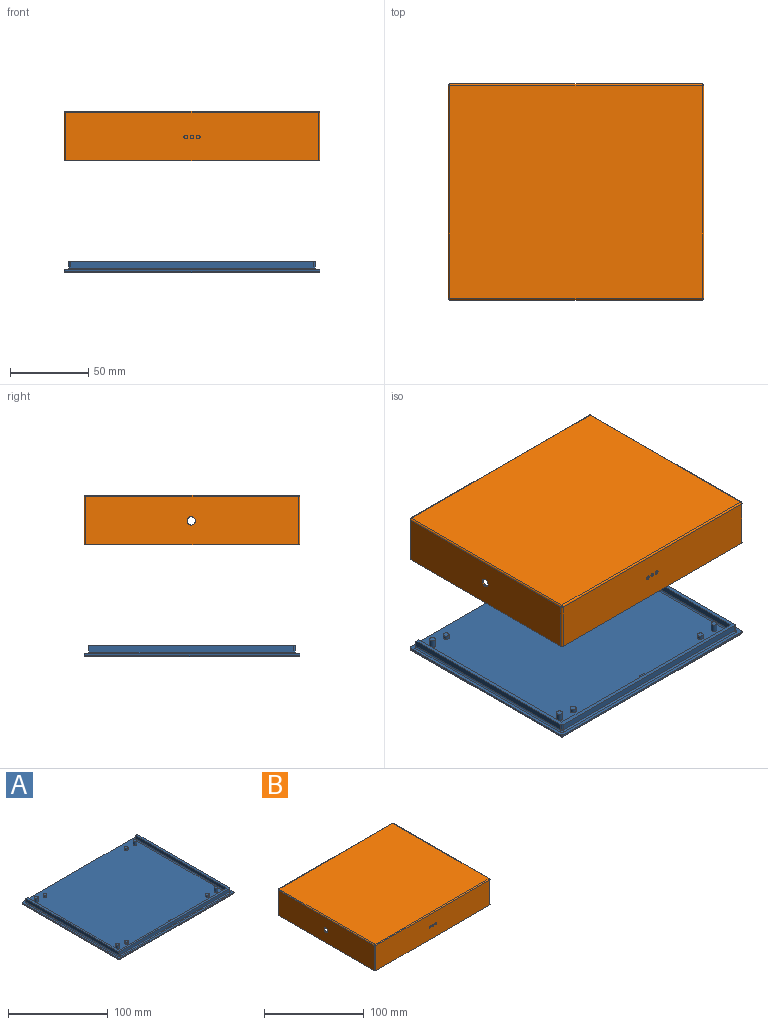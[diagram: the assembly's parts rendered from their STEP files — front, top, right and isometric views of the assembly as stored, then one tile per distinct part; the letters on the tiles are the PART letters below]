
ASSEMBLY  parts=2 mates=2
PART A: 65 faces, bbox 163.4x138x7 mm
  f0: cylinder r=0.99mm len=74.2mm, axis (-1,0,0), area 114.7mm2, adj f1,f9,f26,f39
  f1: plane 163.4x138mm, normal (0,0,1), area 20586.2mm2, adj f0,f2,f3,f4,f5,f7,f11,f19
  f2: plane 161.42x1mm, normal (0,1,0), area 161.4mm2, adj f1,f18,f27,f37
  f3: plane 136.02x1.01mm, normal (-1,0,0), area 137.3mm2, adj f1,f32,f35,f36,f37
  f4: plane 161.42x1.01mm, normal (0,-1,0), area 162.9mm2, adj f1,f29,f32,f33
  f5: plane 136.02x1.01mm, normal (1,0,0), area 137.3mm2, adj f1,f27,f28,f29,f30
  f6: plane 161.42x136.01mm, normal (0,0,-1), area 21954.5mm2, adj f18,f30,f33,f35
  f7: plane 5x4.48mm, normal (0,1,0), area 12.9mm2, adj f1,f8,f14,f15,f19,f24
  f8: plane 129.5x4.01mm, normal (-1,0,0), area 519.2mm2, adj f7,f9,f15,f24
  f9: plane 152.4x4.01mm, normal (0,1,0), area 605.1mm2, adj f0,f8,f10,f15,f25,f38,f39,f40
  f10: plane 129.5x4.01mm, normal (1,0,0), area 519.2mm2, adj f9,f11,f15,f26
  f11: plane 5x4.48mm, normal (0,1,0), area 12.9mm2, adj f1,f10,f12,f15,f23,f26
  f12: plane 131x4.01mm, normal (-1,0,0), area 525.2mm2, adj f11,f15,f16,f23
  f13: plane 155.4x4.01mm, normal (0,-1,0), area 623.1mm2, adj f15,f16,f17,f21
  f14: plane 131x4.01mm, normal (1,0,0), area 525.2mm2, adj f7,f15,f17,f19
  f15: plane 157.4x132mm, normal (0,0,1), area 1040.6mm2, adj f7,f8,f9,f10,f11,f12,f13,f14
  f16: cylinder r=1mm len=4.01mm, axis (0,0,-1), area 6.3mm2, adj f12,f13,f15,f22
  f17: cylinder r=1mm len=4.01mm, axis (0,0,1), area 6.3mm2, adj f13,f14,f15,f20
  f18: cylinder r=1mm len=161.42mm, axis (1,0,0), area 253.6mm2, adj f2,f6,f28,f36
  f19: cylinder r=0.99mm len=131mm, axis (0,1,0), area 203.8mm2, adj f1,f7,f14,f20
  f20: torus R=1.99mm, axis (0,0,1), area 3.3mm2, adj f1,f17,f19,f21
  f21: cylinder r=0.99mm len=155.4mm, axis (1,0,0), area 241.8mm2, adj f1,f13,f20,f22
  f22: torus R=1.99mm, axis (0,0,1), area 3.3mm2, adj f1,f16,f21,f23
  f23: cylinder r=0.99mm len=131mm, axis (0,-1,0), area 203.8mm2, adj f1,f11,f12,f22
  f24: cylinder r=0.99mm len=129.5mm, axis (0,-1,0), area 200.7mm2, adj f1,f7,f8,f25
  f25: cylinder r=0.99mm len=74.2mm, axis (-1,0,0), area 114.7mm2, adj f1,f9,f24,f38
  f26: cylinder r=0.99mm len=129.5mm, axis (0,1,0), area 200.7mm2, adj f0,f1,f10,f11
  f27: cylinder r=0.99mm len=1mm, axis (0,0,1), area 1.6mm2, adj f1,f2,f5,f28
  f28: torus R=0.01mm, axis (-1,0,0), area 1.6mm2, adj f5,f18,f27,f30
  f29: cylinder r=0.99mm len=1.01mm, axis (0,0,-1), area 1.6mm2, adj f1,f4,f5,f31
  f30: cylinder r=0.99mm len=136.01mm, axis (0,-1,0), area 211.6mm2, adj f5,f6,f28,f31
  f31: sphere r=0.99mm, area 1.5mm2, adj f29,f30,f33
  f32: cylinder r=0.99mm len=1.01mm, axis (0,0,1), area 1.6mm2, adj f1,f3,f4,f34
  f33: cylinder r=0.99mm len=161.42mm, axis (-1,0,0), area 251.2mm2, adj f4,f6,f31,f34
  f34: sphere r=0.99mm, area 1.5mm2, adj f32,f33,f35
  f35: cylinder r=0.99mm len=136.01mm, axis (0,1,0), area 211.6mm2, adj f3,f6,f34,f36
  f36: torus R=0.01mm, axis (-1,0,0), area 1.6mm2, adj f3,f18,f35,f37
  f37: cylinder r=0.99mm len=1mm, axis (0,0,-1), area 1.6mm2, adj f1,f2,f3,f36
  f38: plane 3.49x1.99mm, normal (1,0,0), area 6.7mm2, adj f1,f9,f25,f42,f43
  f39: plane 3.49x1.99mm, normal (-1,0,0), area 6.7mm2, adj f0,f1,f9,f44,f45
  f40: plane 3.49x3mm, normal (0,0,1), area 10.5mm2, adj f9,f43,f44,f48
  f41: plane 3x1.99mm, normal (0,1,0), area 6mm2, adj f1,f42,f45,f48
  f42: cylinder r=0.5mm len=1.99mm, axis (0,0,-1), area 1.6mm2, adj f1,f38,f41,f46
  f43: cylinder r=0.5mm len=3.49mm, axis (0,1,0), area 2.7mm2, adj f9,f38,f40,f46
  f44: cylinder r=0.5mm len=3.49mm, axis (0,-1,0), area 2.7mm2, adj f9,f39,f40,f47
  f45: cylinder r=0.5mm len=1.99mm, axis (0,0,1), area 1.6mm2, adj f1,f39,f41,f47
  f46: sphere r=0.5mm, area 0.2mm2, adj f42,f43,f48
  f47: sphere r=0.5mm, area 0.5mm2, adj f44,f45,f48
  f48: cylinder r=0.5mm len=3mm, axis (-1,0,0), area 2.4mm2, adj f40,f41,f46,f47
  f49: cylinder r=1.85mm len=3.7mm, axis (0,0,-1), area 29.1mm2, adj f1,f50
  f50: plane 3.7x3.7mm, normal (0,0,1), area 10.8mm2, adj f49
  f51: cylinder r=1.85mm len=3.7mm, axis (0,0,-1), area 29.1mm2, adj f1,f52
  f52: plane 3.7x3.7mm, normal (0,0,1), area 10.8mm2, adj f51
  f53: cylinder r=1.85mm len=3.7mm, axis (0,0,-1), area 29.1mm2, adj f1,f54
  f54: plane 3.7x3.7mm, normal (0,0,1), area 10.8mm2, adj f53
  f55: cylinder r=1.85mm len=3.7mm, axis (0,0,-1), area 29.1mm2, adj f1,f56
  f56: plane 3.7x3.7mm, normal (0,0,1), area 10.8mm2, adj f55
  f57: cylinder r=1.85mm len=5mm, axis (0,0,-1), area 58.1mm2, adj f1,f58
  f58: plane 3.7x3.7mm, normal (0,0,1), area 10.8mm2, adj f57
  f59: cylinder r=1.85mm len=5mm, axis (0,0,-1), area 58.1mm2, adj f1,f60
  f60: plane 3.7x3.7mm, normal (0,0,1), area 10.8mm2, adj f59
  f61: cylinder r=1.85mm len=5mm, axis (0,0,-1), area 58.1mm2, adj f1,f62
  f62: plane 3.7x3.7mm, normal (0,0,1), area 10.8mm2, adj f61
  f63: cylinder r=1.85mm len=5mm, axis (0,0,-1), area 58.1mm2, adj f1,f64
  f64: plane 3.7x3.7mm, normal (0,0,1), area 10.8mm2, adj f63
PART B: 39 faces, bbox 163.4x138x31.8 mm
  f0: plane 10.35x1mm, normal (0,0,-1), area 10.3mm2, adj f2,f8,f28,f32
  f1: plane 14.39x1mm, normal (0,0,-1), area 14.4mm2, adj f2,f8,f25,f29
  f2: plane 161.42x30.76mm, normal (0,1,0), area 4734.1mm2, adj f0,f1,f11,f15,f21,f24,f25,f26
  f3: plane 136.02x30.76mm, normal (-1,0,0), area 4161.3mm2, adj f11,f18,f22,f24,f34
  f4: plane 161.42x30.76mm, normal (0,-1,0), area 4952mm2, adj f11,f13,f17,f18,f36,f37,f38
  f5: plane 136.02x30.76mm, normal (1,0,0), area 4160mm2, adj f11,f13,f15,f16,f35
  f6: plane 161.42x136.02mm, normal (0,0,1), area 21956mm2, adj f16,f17,f21,f22
  f7: plane 136x30.75mm, normal (1,0,0), area 4159.4mm2, adj f8,f10,f11,f12,f34
  f8: plane 161.4x30.75mm, normal (0,-1,0), area 4732mm2, adj f0,f1,f7,f9,f11,f12,f25,f26
  f9: plane 136x30.75mm, normal (-1,0,0), area 4158.2mm2, adj f8,f10,f11,f12,f35
  f10: plane 161.4x30.75mm, normal (0,1,0), area 4949.9mm2, adj f7,f9,f11,f12,f36,f37,f38
  f11: plane 163.4x138mm, normal (0,0,-1), area 537.4mm2, adj f2,f3,f4,f5,f7,f8,f9,f10
  f12: plane 161.4x136mm, normal (0,0,-1), area 21950.4mm2, adj f7,f8,f9,f10
  f13: cylinder r=0.99mm len=30.76mm, axis (0,0,-1), area 47.9mm2, adj f4,f5,f11,f14
  f14: sphere r=0.99mm, area 1.5mm2, adj f13,f16,f17
  f15: cylinder r=0.99mm len=30.76mm, axis (0,0,1), area 47.9mm2, adj f2,f5,f11,f19
  f16: cylinder r=0.99mm len=136.02mm, axis (0,1,0), area 211.6mm2, adj f5,f6,f14,f19
  f17: cylinder r=0.99mm len=161.42mm, axis (1,0,0), area 251.2mm2, adj f4,f6,f14,f20
  f18: cylinder r=0.99mm len=30.76mm, axis (0,0,1), area 47.9mm2, adj f3,f4,f11,f20
  f19: sphere r=0.99mm, area 1.5mm2, adj f15,f16,f21
  f20: sphere r=0.99mm, area 1.5mm2, adj f17,f18,f22
  f21: cylinder r=0.99mm len=161.42mm, axis (-1,0,0), area 251.2mm2, adj f2,f6,f19,f23
  f22: cylinder r=0.99mm len=136.02mm, axis (0,-1,0), area 211.6mm2, adj f3,f6,f20,f23
  f23: sphere r=0.99mm, area 1.5mm2, adj f21,f22,f24
  f24: cylinder r=0.99mm len=30.76mm, axis (0,0,-1), area 47.9mm2, adj f2,f3,f11,f23
  f25: plane 5.19x1mm, normal (1,0,0), area 5.2mm2, adj f1,f2,f8,f27
  f26: plane 5.19x1mm, normal (-1,0,0), area 5.2mm2, adj f2,f8,f11,f27
  f27: plane 14.65x1mm, normal (0,0,-1), area 14.7mm2, adj f2,f8,f25,f26
  f28: plane 9.71x1mm, normal (1,0,0), area 9.7mm2, adj f0,f2,f8,f30
  f29: plane 9.71x1mm, normal (-1,0,0), area 9.7mm2, adj f1,f2,f8,f30
  f30: plane 11.54x1mm, normal (0,0,-1), area 11.5mm2, adj f2,f8,f28,f29
  f31: plane 4.45x1mm, normal (1,0,0), area 4.4mm2, adj f2,f8,f11,f33
  f32: plane 4.45x1mm, normal (-1,0,0), area 4.4mm2, adj f0,f2,f8,f33
  f33: plane 9.67x1mm, normal (0,0,-1), area 9.7mm2, adj f2,f8,f31,f32
  f34: cylinder r=2.68mm len=5.36mm, axis (1,0,0), area 16.8mm2, adj f3,f7
  f35: cylinder r=2.75mm len=5.51mm, axis (-1,0,0), area 17.3mm2, adj f5,f9
  f36: cylinder r=1.18mm len=2.36mm, axis (0,-1,0), area 7.4mm2, adj f4,f10
  f37: cylinder r=1.18mm len=2.36mm, axis (0,-1,0), area 7.4mm2, adj f4,f10
  f38: cylinder r=1.18mm len=2.36mm, axis (0,-1,0), area 7.4mm2, adj f4,f10
PLACE A t=(-51.58,41.84,0)mm
PLACE B t=(-51.58,41.84,44.06)mm
MATE planar B.f36 <-> A.f4  axis (0,-1,0) through (-51.58,-27.67,84.84)mm
MATE planar B.f5 <-> A.f5  axis (1,0,0) through (30.12,41.33,84.84)mm
